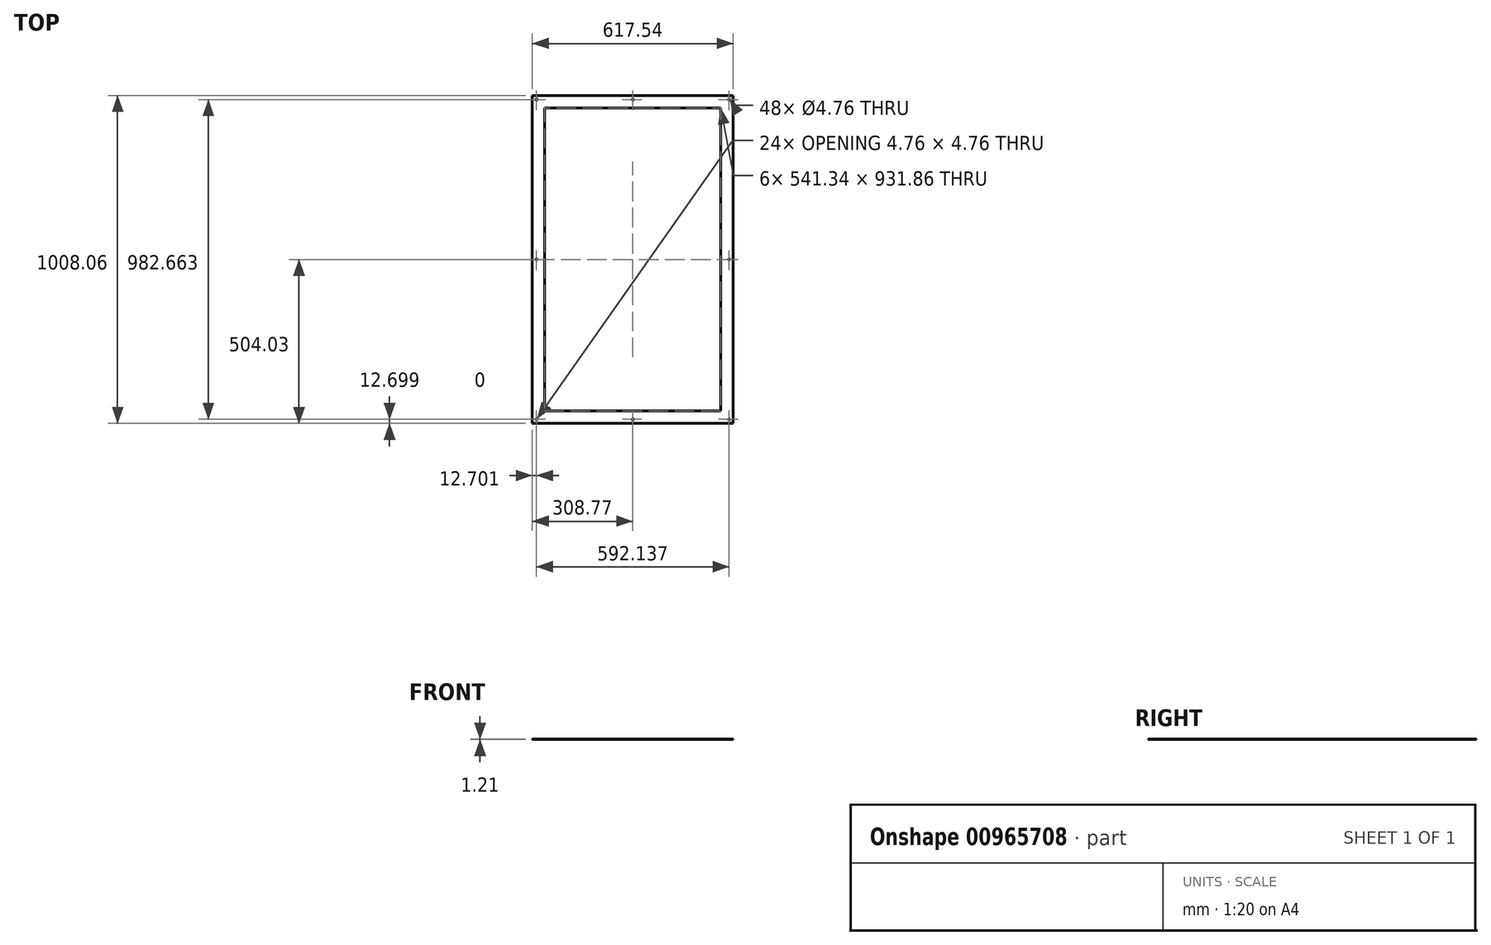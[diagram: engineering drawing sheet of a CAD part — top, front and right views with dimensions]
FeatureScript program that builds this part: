
annotation { "Feature Type Name" : "Feature", "Feature Type Description" : "" }
export const myFeature = defineFeature(function(context is Context, id is Id, definition is map)
    precondition{}
    {
        {
            var Q0;
            Q0=qCreatedBy(makeId("Top.planeOp"),FACE);
            var sketch = newSketch(context, id + "F0", { "sketchPlane" : qUnion([Q0])});
            skLineSegment(sketch, "E0.bottom", {"start": v(270.67, 465.93) * mm, "end": v(-270.67, 465.93) * mm});
            skLineSegment(sketch, "E0.top", {"start": v(270.67, -465.93) * mm, "end": v(-270.67, -465.93) * mm});
            skLineSegment(sketch, "E0.left", {"start": v(270.67, 465.93) * mm, "end": v(270.67, -465.93) * mm});
            skLineSegment(sketch, "E0.right", {"start": v(-270.67, 465.93) * mm, "end": v(-270.67, -465.93) * mm});
            skPoint(sketch, "E0.middle", {"position": v(0, 0) * mm});
            skLineSegment(sketch, "E1.0", {"start": v(-308.77, 504.03) * mm, "end": v(-308.77, -504.03) * mm});
            skLineSegment(sketch, "E1.1", {"start": v(308.77, 504.03) * mm, "end": v(-308.77, 504.03) * mm});
            skLineSegment(sketch, "E1.2", {"start": v(308.77, 504.03) * mm, "end": v(308.77, -504.03) * mm});
            skLineSegment(sketch, "E1.3", {"start": v(308.77, -504.03) * mm, "end": v(-308.77, -504.03) * mm});
            skSolve(sketch);
        }
        {
            var Q0;
            Q0=makeQuery(id+"F0.imprint","IMPRINT",FACE,{"disambiguationData":[TD([[makeQuery(id+"F0.imprint","IMPRINT",EDGE,{"derivedFrom":sQuery(id+"F0.wireOp",EDGE,"E0.bottom")}),-1.0]])]});
            extrude(context, id + "F1", {"entities" : qUnion([Q0]), "depth" : 1.21 * mm, "offsetDistance" : 25.4 * mm});
        }
        {
            var Q0;
            Q0=makeQuery(id+"F1.opExtrude","CAP_FACE",FACE,{"disambiguationData":[OSD([sQuery(id+"F0.wireOp",EDGE,"E0.bottom"),sQuery(id+"F0.wireOp",EDGE,"E0.top"),sQuery(id+"F0.wireOp",EDGE,"E0.left"),sQuery(id+"F0.wireOp",EDGE,"E0.right"),sQuery(id+"F0.wireOp",EDGE,"E1.0"),sQuery(id+"F0.wireOp",EDGE,"E1.1"),sQuery(id+"F0.wireOp",EDGE,"E1.2"),sQuery(id+"F0.wireOp",EDGE,"E1.3")])],"isStart":true});
            var sketch = newSketch(context, id + "F2", { "sketchPlane" : qUnion([Q0])});
            skLineSegment(sketch, "E2.0", {"start": v(296.07, 491.33) * mm, "end": v(-296.07, 491.33) * mm});
            skLineSegment(sketch, "E2.1", {"start": v(296.07, -491.33) * mm, "end": v(296.07, 491.33) * mm});
            skLineSegment(sketch, "E2.2", {"start": v(296.07, -491.33) * mm, "end": v(-296.07, -491.33) * mm});
            skLineSegment(sketch, "E2.3", {"start": v(-296.07, -491.33) * mm, "end": v(-296.07, 491.33) * mm});
            skPoint(sketch, "E3", {"position": v(-296.07, 491.33) * mm});
            skPoint(sketch, "E4", {"position": v(296.07, 491.33) * mm});
            skPoint(sketch, "E5", {"position": v(-296.07, -491.33) * mm});
            skPoint(sketch, "E6", {"position": v(296.07, -491.33) * mm});
            skPoint(sketch, "E7", {"position": v(-296.07, 0) * mm});
            skPoint(sketch, "E8", {"position": v(296.07, 0) * mm});
            skPoint(sketch, "E9", {"position": v(0, -491.33) * mm});
            skPoint(sketch, "E10", {"position": v(0, 491.33) * mm});
            skSolve(sketch);
        }
        {
            var Q0;
            Q0=sQuery(id+"F2.wireOp",VERTEX,"E3");
            var Q1;
            Q1=sQuery(id+"F2.wireOp",VERTEX,"E10");
            var Q2;
            Q2=sQuery(id+"F2.wireOp",VERTEX,"E4");
            var Q3;
            Q3=sQuery(id+"F2.wireOp",VERTEX,"E8");
            var Q4;
            Q4=sQuery(id+"F2.wireOp",VERTEX,"E6");
            var Q5;
            Q5=sQuery(id+"F2.wireOp",VERTEX,"E9");
            var Q6;
            Q6=sQuery(id+"F2.wireOp",VERTEX,"E5");
            var Q7;
            Q7=sQuery(id+"F2.wireOp",VERTEX,"E7");
            var Q8;
            Q8=makeQuery(id+"F1.opExtrude","SWEPT_BODY",BODY,{"disambiguationData":[OSD([sQuery(id+"F0.wireOp",EDGE,"E0.bottom"),sQuery(id+"F0.wireOp",EDGE,"E0.top"),sQuery(id+"F0.wireOp",EDGE,"E0.left"),sQuery(id+"F0.wireOp",EDGE,"E0.right"),sQuery(id+"F0.wireOp",EDGE,"E1.0"),sQuery(id+"F0.wireOp",EDGE,"E1.1"),sQuery(id+"F0.wireOp",EDGE,"E1.2"),sQuery(id+"F0.wireOp",EDGE,"E1.3")])]});
            hole(context, id + "F3", {"style" : HoleStyle.SIMPLE, "endStyle" : HoleEndStyle.THROUGH, "holeDiameter" : 4.76 * mm, "majorDiameter" : 6.35 * mm, "isTappedThrough" : true, "tappedDepth" : 12.7 * mm, "tapClearance" : 3, "locations" : qUnion([Q0, Q1, Q2, Q3, Q4, Q5, Q6, Q7]), "scope" : qUnion([Q8])});
        }
    });
